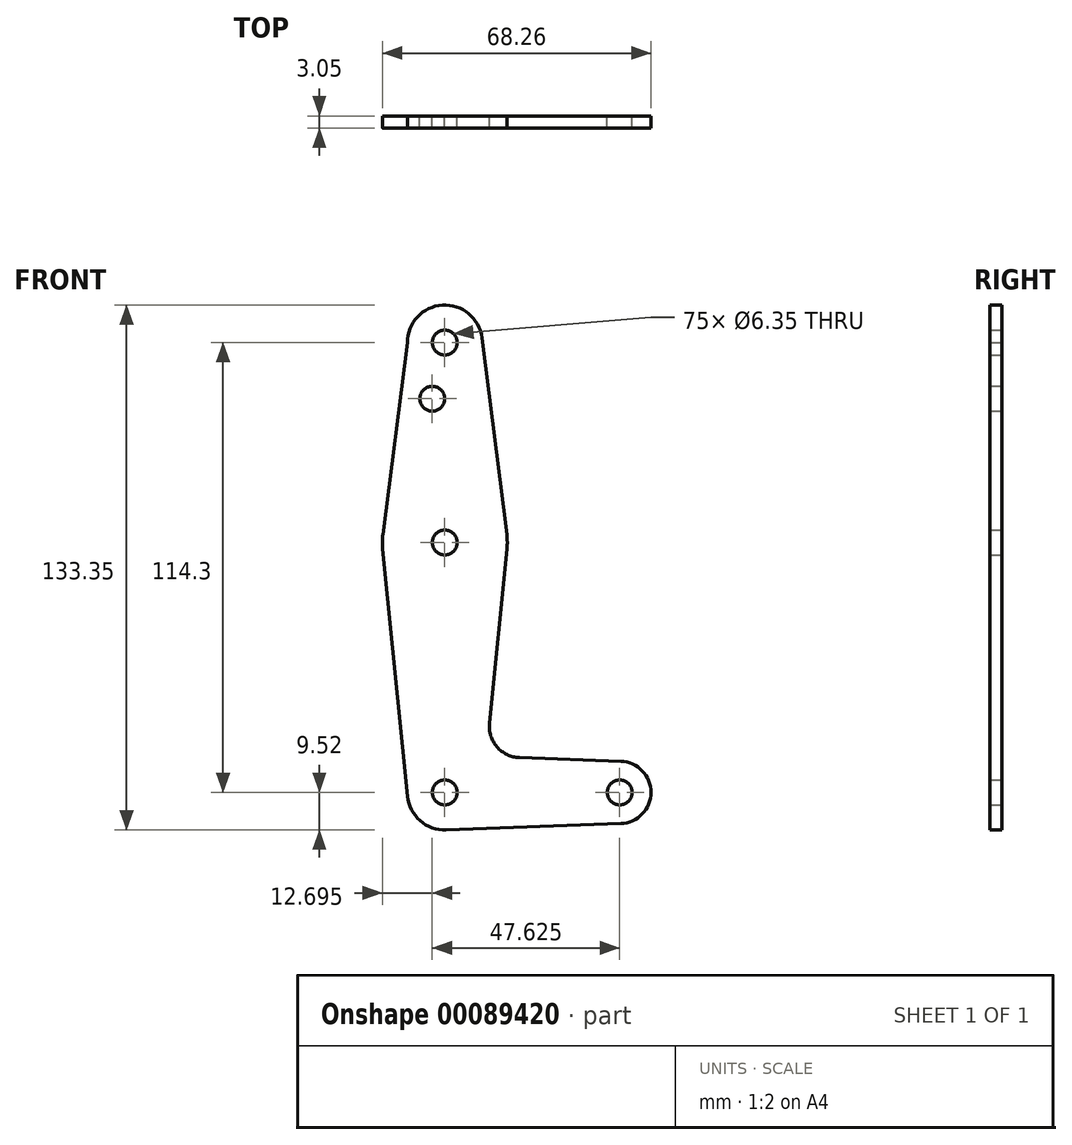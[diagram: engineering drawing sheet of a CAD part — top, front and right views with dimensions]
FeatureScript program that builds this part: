
annotation { "Feature Type Name" : "Feature", "Feature Type Description" : "" }
export const myFeature = defineFeature(function(context is Context, id is Id, definition is map)
    precondition{}
    {
        {
            var Q0;
            Q0=qCreatedBy(makeId("Front.planeOp"),FACE);
            var sketch = newSketch(context, id + "F0", { "sketchPlane" : qUnion([Q0])});
            skLineSegment(sketch, "E0", {"start": v(0, 63.5) * mm, "end": v(0, 0) * mm, "construction": true});
            skLineSegment(sketch, "E1", {"start": v(0, 0) * mm, "end": v(44.45, 0) * mm, "construction": true});
            skCircle(sketch, "E2", {"center": v(0, 63.5) * mm, "radius": 15.88 * mm});
            skCircle(sketch, "E3", {"center": v(0, 114.3) * mm, "radius": 9.53 * mm});
            skCircle(sketch, "E4", {"center": v(0, 0) * mm, "radius": 9.53 * mm});
            skCircle(sketch, "E5", {"center": v(44.45, 0) * mm, "radius": 7.94 * mm});
            skLineSegment(sketch, "E6", {"start": v(0, 114.3) * mm, "end": v(0, 63.5) * mm, "construction": true});
            skCircle(sketch, "E7", {"center": v(0, 114.3) * mm, "radius": 3.18 * mm});
            skCircle(sketch, "E8", {"center": v(0, 63.5) * mm, "radius": 3.18 * mm});
            skCircle(sketch, "E9", {"center": v(0, 0) * mm, "radius": 3.18 * mm});
            skCircle(sketch, "E10", {"center": v(44.45, 0) * mm, "radius": 3.18 * mm});
            skLineSegment(sketch, "E11", {"start": v(44.73, -7.93) * mm, "end": v(0, -9.53) * mm});
            skCircle(sketch, "E12", {"center": v(-3.18, 100.03) * mm, "radius": 3.18 * mm});
            skPoint(sketch, "E13.newPointA", {"position": v(9.57, 0) * mm});
            skPoint(sketch, "E13.newPointB", {"position": v(0, 9.53) * mm});
            skLineSegment(sketch, "E14", {"start": v(-9.53, 114.3) * mm, "end": v(-15.75, 65.5) * mm});
            skLineSegment(sketch, "E15", {"start": v(9.45, 115.5) * mm, "end": v(15.75, 65.48) * mm});
            skLineSegment(sketch, "E16", {"start": v(44.73, 7.93) * mm, "end": v(18.97, 8.85) * mm});
            skLineSegment(sketch, "E17", {"start": v(15.8, 61.91) * mm, "end": v(11.34, 17.6) * mm});
            skArc(sketch, "E18.filletArc", {"start": v(11.34, 17.6) * mm, "mid": v(13.26, 11.57) * mm, "end": v(18.97, 8.85) * mm});
            skLineSegment(sketch, "E19", {"start": v(-15.8, 61.91) * mm, "end": v(-9.48, -0.95) * mm});
            skSolve(sketch);
        }
        {
            var Q0;
            Q0=makeQuery(id+"F0.imprint","IMPRINT",FACE,{"disambiguationData":[TD([[makeQuery(id+"F0.imprint","IMPRINT",EDGE,{"derivedFrom":sQuery(id+"F0.wireOp",EDGE,"E7")}),-1.0]])]});
            var Q1;
            Q1=makeQuery(id+"F0.imprint","IMPRINT",FACE,{"disambiguationData":[TD([[makeQuery(id+"F0.imprint","IMPRINT",EDGE,{"derivedFrom":sQuery(id+"F0.wireOp",EDGE,"E12")}),-1.0]])]});
            var Q2;
            Q2=makeQuery(id+"F0.imprint","IMPRINT",FACE,{"disambiguationData":[TD([[makeQuery(id+"F0.imprint","IMPRINT",EDGE,{"derivedFrom":sQuery(id+"F0.wireOp",EDGE,"E8")}),-1.0]])]});
            var Q3;
            {var subQ6=sQuery(id+"F0.wireOp",EDGE,"E16");Q3=makeQuery(id+"F0.imprint","IMPRINT",FACE,{"disambiguationData":[TD([[makeQuery(id+"F0.imprint","IMPRINT",EDGE,{"derivedFrom":subQ6}),1.0]])]});}
            var Q4;
            Q4=makeQuery(id+"F0.imprint","IMPRINT",FACE,{"disambiguationData":[TD([[makeQuery(id+"F0.imprint","IMPRINT",EDGE,{"derivedFrom":sQuery(id+"F0.wireOp",EDGE,"E9")}),-1.0]])]});
            var Q5;
            Q5=makeQuery(id+"F0.imprint","IMPRINT",FACE,{"disambiguationData":[TD([[makeQuery(id+"F0.imprint","IMPRINT",EDGE,{"derivedFrom":sQuery(id+"F0.wireOp",EDGE,"E10")}),-1.0]])]});
            extrude(context, id + "F1", {"entities" : qUnion([Q0, Q1, Q2, Q3, Q4, Q5]), "depth" : 3.05 * mm});
        }
    });
